# Revit family: Tub_Filler-American_Standard-Delancey-T052900_Series
name_source: partatom
category: Plumbing Fixtures
revit_build: Autodesk Revit 2018 (Build: 20170223_1515(x64)
units: mm (PartAtom-declared; Revit-internal decimal feet)

## family parameters
Always vertical = No
Cut with Voids When Loaded = No
OmniClass Number = 23.45.55.14
OmniClass Title = Single Faucets
Part Type = Normal
Room Calculation Point = No
Round Connector Dimension = Use Diameter
Shared = Yes
Work Plane-Based = Yes

## types (4) — shared parameters
ADA Compliant = Yes
Assembly Code = D2020300
CW Connection = Yes
CWFU = 3
Cold Water Connection Diameter = 1/2"
Default Elevation = 0"
Description = Delancey Roman Tub Faucet for Flash Rough-in Valves
HW Connection = Yes
HWFU = 3
Height = 7 5/8"
Hot Water Connection Diameter = 1/2"
IAPMO Compliance = Product meet or exceeds ASME A112.18.1, CSA B125.1
Installation Type = Deck Mounted
Length = 12"
Manufacturer = American Standard
Price = Prices may vary. Please consult Manufacturer Representative for most up-to-date price list.
Product Documentation Link = https://www.americanstandard-us.com
Product Page URL = https://www.americanstandard-us.com
Revised Date = 05/03/2021
URL = http://www.americanstandard-us.com
Vent Connection = No
Waste Connection = No
Width = 10"
zero-valued in all types: WFU

## per-type parameters (varying)
| type | Finish | Handle Type | Material |
| T052900.002 | Metal-American_Standard-002-Polished_Chrome | Handle : 002 | Metal-American_Standard-002-Polished_Chrome |
| T052900.295 | Metal-American_Standard-295-Brushed_Nickel | Handle : 295 | Metal-American Standard-295-Brushed Nickel |
| T052900.013 | Metal-American_Standard-013-Polished_Nickel | Handle : 013 | Metal-American Standard-013-Polished Nickel |
| T052900.278 | Metal-American_Standard-278-Legacy_Bronze | Handle : 278 | Metal-American Standard-278-Legacy Bronze |

note: column(s) folded — value = type name in every type: Model

## geometry (parser evidence)
native form markers: Sweep x3
no freeform markers — native parametric forms only
